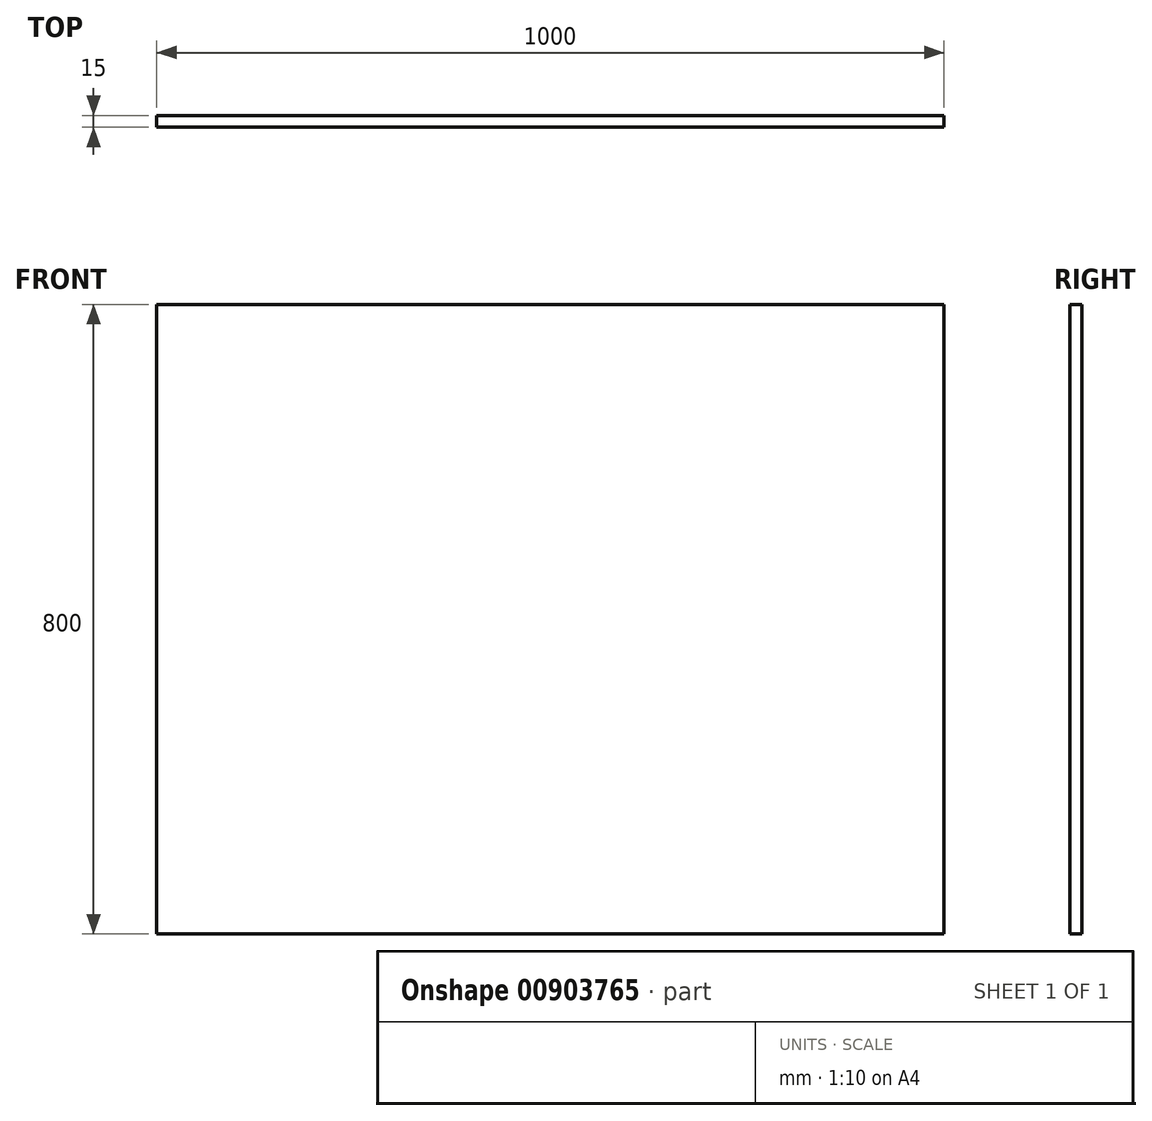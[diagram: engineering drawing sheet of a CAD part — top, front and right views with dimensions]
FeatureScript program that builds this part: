
annotation { "Feature Type Name" : "Feature", "Feature Type Description" : "" }
export const myFeature = defineFeature(function(context is Context, id is Id, definition is map)
    precondition{}
    {
        {
            var Q0;
            Q0=qCreatedBy(makeId("Front.planeOp"),FACE);
            var sketch = newSketch(context, id + "F0", { "sketchPlane" : qUnion([Q0])});
            skLineSegment(sketch, "E0.bottom", {"start": v(-500, 400) * mm, "end": v(500, 400) * mm});
            skLineSegment(sketch, "E0.top", {"start": v(-500, -400) * mm, "end": v(500, -400) * mm});
            skLineSegment(sketch, "E0.left", {"start": v(-500, 400) * mm, "end": v(-500, -400) * mm});
            skLineSegment(sketch, "E0.right", {"start": v(500, 400) * mm, "end": v(500, -400) * mm});
            skSolve(sketch);
        }
        {
            var Q0;
            Q0=makeQuery(id+"F0.imprint","IMPRINT",FACE,{"disambiguationData":[TD([[makeQuery(id+"F0.imprint","IMPRINT",EDGE,{"derivedFrom":sQuery(id+"F0.wireOp",EDGE,"E0.bottom")}),-1.0]])]});
            extrude(context, id + "F1", {"entities" : qUnion([Q0]), "depth" : 15 * mm, "offsetDistance" : 25 * mm});
        }
    });
